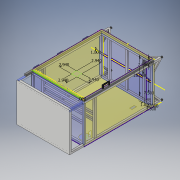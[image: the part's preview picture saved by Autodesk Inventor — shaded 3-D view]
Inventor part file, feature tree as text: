
AUTODESK INVENTOR PART (.ipt)
format: ipt  version: 2019 (Build 230136000, 136)  size: 635,904 bytes
history: native  units: in
note: dims shown in document units (in); Inventor stores cm internally (conversion verified against a paired STEP export)
features: sketch x35, extrude x27, mirror x21, other x9, hole x8, projected_geometry x3, plane x2
ambient origin geometry x8: Origin, YZ Plane, XZ Plane, XY Plane, X Axis, Y Axis, Z Axis, Center Point
bodies: Solid12 (feature_tree), Solid13 (feature_tree)
feature tree (105):
  other  "T-slot rails"
  extrude  "Extrusion1"  Depth=20.0in
  mirror  "Mirror1"
  extrude  "Extrusion2"  Depth=1.0in TaperAngle=0.0deg
  mirror  "Mirror2"
  extrude  "Extrusion3"  Depth=1.0in TaperAngle=0.0deg
  mirror  "Mirror3"
  mirror  "Mirror4"
  plane  "Work Plane1"
  mirror  "Mirror5"
  extrude  "Extrusion4"  TaperAngle=0.0deg  [1 undecoded]
  extrude  "Extrusion5"  Depth=0.5in
  mirror  "Mirror6"
  mirror  "Mirror7"
  extrude  "Extrusion6"  Depth=0.5in
  extrude  "Extrusion7"  Depth=1.0in
  extrude  "Extrusion8"  Depth=0.125in TaperAngle=0.0deg
  mirror  "Mirror8"
  extrude  "Extrusion9"  Depth=0.0625in TaperAngle=0.0deg
  sketch  "Sketch10"  dims[d25=0.0in d26=0.0625in d27=0.0in]
  extrude  "Extrusion12"  TaperAngle=0.0deg  [1 undecoded]
  sketch  "Sketch12"  dims[d28=1.0in d29=0.0in]
  extrude  "Extrusion14"  Depth=1.0in
  extrude  "Extrusion15"  TaperAngle=0.0deg  [1 undecoded]
  mirror  "Mirror10"
  extrude  "Extrusion16"  Depth=1.0in TaperAngle=0.0deg
  extrude  "Extrusion17"  Depth=0.125in TaperAngle=0.0deg
  extrude  "Extrusion18"  TaperAngle=0.0deg  [1 undecoded]
  extrude  "Extrusion19"  Depth=0.5in
  extrude  "Extrusion20"  TaperAngle=0.0deg  [1 undecoded]
  mirror  "Mirror11"
  extrude  "Extrusion23"  Depth=0.5in
  mirror  "Mirror12"
  mirror  "Mirror15"
  extrude  "Extrusion24"  Depth=2.0in
  mirror  "Mirror16"
  mirror  "Mirror17"
  mirror  "Mirror18"
  extrude  "Extrusion25"  TaperAngle=0.0deg  [1 undecoded]
  mirror  "Mirror19"
  mirror  "Mirror20"
  mirror  "Mirror21"
  sketch  "Sketch28"  dims[d64=0.5in d65=2.0in]
  sketch  "Sketch40"  dims[d66=0.5in d67=0.0in d68=0.0in]
  extrude  "Extrusion36"  Depth=3.0in
  hole  "Hole16"  [1 undecoded]
  hole  "Hole17"  [1 undecoded]
  hole  "Hole18"  [1 undecoded]
  hole  "Hole15"  [1 undecoded]
  hole  "Hole22"  [1 undecoded]
  hole  "Hole23"  [1 undecoded]
  hole  "Hole24"  [1 undecoded]
  hole  "Hole25"  [1 undecoded]
  sketch  "Sketch54"  dims[d90=1.0in d91=20.0in d92=1.0in d94=0.0in d95=1.0in d96=13.5in]
  sketch  "Sketch55"  dims[d97=3.5in d98=32.0in]
  extrude  "Extrusion44"  Depth=1.0in
  extrude  "Extrusion45"  Depth=6.0in
  plane  "Work Plane3"
  sketch  "Sketch58"  dims[d125=1.0in d126=1.0in]
  extrude  "Extrusion46"  TaperAngle=90.0deg  [1 undecoded]
  mirror  "Mirror32"
  extrude  "Extrusion47"  Depth=1.0in
  mirror  "Mirror33"
  sketch  "Sketch61"  dims[d132=1.0in d133=1.0in]
  mirror  "Mirror34"
  extrude  "Extrusion48"  Depth=1.0in
  sketch  "Sketch1"  dims[d0=1.0in d1=20.0in]
  sketch  "Sketch2"  dims[d2=14.0in d3=1.0in d4=0.0in]
  other  "More rails"
  sketch  "Sketch3"  dims[d6=1.0in d7=1.0in d8=0.0in]
  other  "Even more rails"
  sketch  "Sketch4"  dims[d9=0.0in d10=0.0in]
  projected_geometry  "Projected Loop1"
  sketch  "Sketch5"  dims[d11=40.0in d12=4.0in d13=0.0in d14=0.0in d15=0.5in]
  other  "Antibration leveling mount"
  sketch  "Sketch6"  dims[d16=0.5in d17=0.5in]
  other  "0.125 in. panel"
  sketch  "Sketch8"  dims[d18=0.8in d19=0.0in d20=1.0in]
  sketch  "Sketch9"  dims[d21=0.2in d22=0.0in d23=0.125in d24=0.0in]
  sketch  "Sketch13"  dims[d31=1.0in d32=0.0in d33=1.0in]
  projected_geometry  "Projected Loop2"
  projected_geometry  "Projected Loop3"
  other  "Door rails"
  sketch  "Sketch14"  dims[d35=0.0in d36=0.0in]
  other  "Door handle"
  sketch  "Sketch16"  dims[d37=1.0in d38=1.0in d39=0.0in]
  other  "Door hinges"
  sketch  "Sketch17"  dims[d42=1.0in d45=0.125in d46=0.0in]
  other  "0.060 in. panel"
  sketch  "Sketch23"  dims[d57=0.0625in d58=0.0in d59=0.5in]
  sketch  "Sketch25"  dims[d60=2.0in d61=0.0in]
  sketch  "Sketch26"  dims[d62=3.0in d63=0.5in]
  sketch  "Sketch41"  dims[d69=0.0625in d70=0.0in d71=3.0in]
  sketch  "Sketch48"  dims[d72=2.0in d73=3.0in]
  sketch  "Sketch50"  dims[d74=3.0in d75=2.0in]
  sketch  "Sketch51"  dims[d76=0.5in d77=0.0in d78=1.0in d79=0.0in]
  sketch  "Sketch52"  dims[d80=1.0in d81=20.0in]
  sketch  "Sketch53"  dims[d82=1.0in d83=0.0in]
  sketch  "Sketch56"  dims[d120=1.0in d121=1.0in]
  sketch  "Sketch57"  dims[d122=8.0in d123=0.0in d124=6.0in]
  sketch  "Sketch59"  dims[d127=1.0in d128=0.0in d129=6.0in]
  sketch  "Sketch60"  dims[d130=1.0in d131=90.0deg]
  sketch  "Sketch62"  dims[d134=1.0in d135=0.0in d172=1.0in d173=1.0in d174=29.0in d175=0.0in d260=5.0in d261=0.38in d262=0.385in d263=0.25in d264=0.5635in d265=0.536in d266=0.8108in d267=5.0in d268=0.38in d269=0.385in d270=0.25in d271=0.5635in d272=0.536in d273=0.8108in d274=5.0in d275=0.38in d276=0.385in d277=0.25in d278=0.5635in d279=3.4375in d280=0.8108in d281=5.1in d282=0.38in d283=0.385in d284=0.25in d285=0.5635in d286=3.4375in d287=0.8108in d316=0.177in d317=0.75in d318=0.37in d319=0.25in d320=90.0deg d321=3.4375in d322=0.8108in d323=0.177in d324=0.75in d325=0.37in d326=0.25in d327=90.0deg d328=3.4375in d329=0.8108in d330=0.177in d331=0.75in d332=0.37in d333=0.25in d334=90.0deg d335=3.4375in d336=0.8108in d337=0.177in d338=0.75in d339=0.37in d340=0.25in d341=90.0deg d342=3.4375in d343=0.8108in d358=1.375in d359=2.63in d360=0.0625in d361=0.0in d362=1.375in d363=2.63in d364=0.0625in d365=0.0in d366=2.94in d367=2.94in d368=2.94in d369=2.94in d370=8.0in d371=0.0in d372=1.0in d373=20.0in d374=0.0in d375=0.125in d376=0.0in d377=7.5in d378=1.5in d379=7.5in d99=1.0in d100=1.0in d101=1.0in d102=0.15in d103=0.25in d104=0.375in d105=0.5635in d106=0.75in d107=0.8108in d108=0.0625in d109=0.75in d110=0.375in d211=1.0in d212=1.0in d213=1.0in d214=0.15in d215=0.25in d216=0.375in d217=0.5635in d218=0.75in d219=0.8108in d220=0.0625in d221=0.75in d222=0.375in d288=0.75in d289=0.8108in d290=0.0625in d291=0.75in d292=0.375in d293=0.375in d294=0.5635in d295=0.75in d296=0.8108in d297=0.0625in d298=0.75in d299=0.375in d300=0.8108in d301=0.0625in d302=0.75in d303=0.375in]
  extrude  "Extrusion22"  Depth=1.0in
  sketch  "Sketch19"  dims[d49=1.0in d50=0.0in d56=0.0in]
note: 15 required parameter values undecoded (feature->parameter linkage not recoverable at this tier; creation-order binding heuristic only, values carry confidence <= 0.55)
